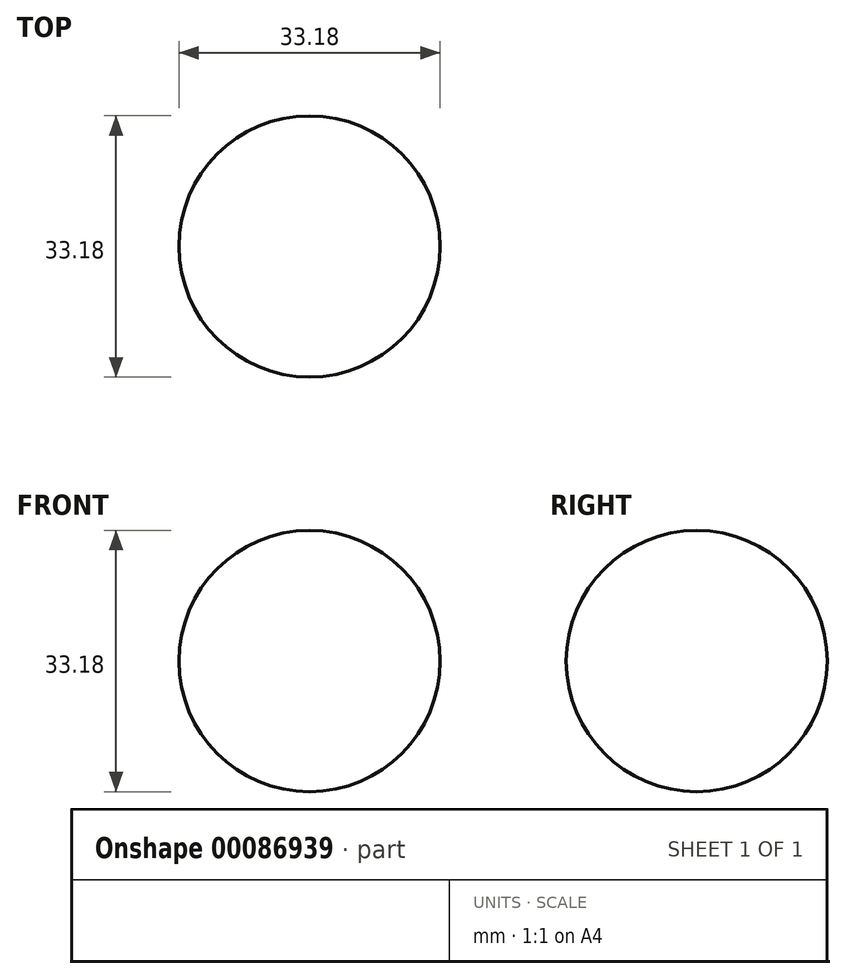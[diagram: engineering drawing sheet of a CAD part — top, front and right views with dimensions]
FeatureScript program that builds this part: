
annotation { "Feature Type Name" : "Feature", "Feature Type Description" : "" }
export const myFeature = defineFeature(function(context is Context, id is Id, definition is map)
    precondition{}
    {
        {
            var Q0;
            Q0=qCreatedBy(makeId("Front.planeOp"),FACE);
            var sketch = newSketch(context, id + "F0", { "sketchPlane" : qUnion([Q0])});
            skLineSegment(sketch, "E0", {"start": v(0, 0) * mm, "end": v(0, -229.17) * mm});
            skArc(sketch, "E1", {"start": v(0, -16.59) * mm, "mid": v(16.59, 0) * mm, "end": v(0, 16.59) * mm});
            skLineSegment(sketch, "E2", {"start": v(0, 0) * mm, "end": v(0, 16.59) * mm});
            skLineSegment(sketch, "E3", {"start": v(0, 0) * mm, "end": v(230.8, 0) * mm});
            skLineSegment(sketch, "E4.bottom", {"start": v(230.8, 13.81) * mm, "end": v(281.42, 13.81) * mm});
            skLineSegment(sketch, "E4.top", {"start": v(230.8, -19.65) * mm, "end": v(281.42, -19.65) * mm});
            skLineSegment(sketch, "E4.left", {"start": v(230.8, 13.81) * mm, "end": v(230.8, -19.65) * mm});
            skLineSegment(sketch, "E4.right", {"start": v(281.42, 13.81) * mm, "end": v(281.42, -19.65) * mm});
            skLineSegment(sketch, "E5.bottom", {"start": v(21.17, -229.17) * mm, "end": v(-17.32, -229.17) * mm});
            skLineSegment(sketch, "E5.top", {"start": v(21.17, -265.04) * mm, "end": v(-17.32, -265.04) * mm});
            skLineSegment(sketch, "E5.left", {"start": v(21.17, -229.17) * mm, "end": v(21.17, -265.04) * mm});
            skLineSegment(sketch, "E5.right", {"start": v(-17.32, -229.17) * mm, "end": v(-17.32, -265.04) * mm});
            skLineSegment(sketch, "E6.bottom", {"start": v(10.62, -238.4) * mm, "end": v(-8.54, -238.4) * mm});
            skLineSegment(sketch, "E6.top", {"start": v(10.62, -256.31) * mm, "end": v(-8.54, -256.31) * mm});
            skLineSegment(sketch, "E6.left", {"start": v(10.62, -238.4) * mm, "end": v(10.62, -256.31) * mm});
            skLineSegment(sketch, "E6.right", {"start": v(-8.54, -238.4) * mm, "end": v(-8.54, -256.31) * mm});
            skSolve(sketch);
        }
        {
            var Q0;
            Q0=qCreatedBy(makeId("Top.planeOp"),FACE);
            var Q1;
            Q1=sQuery(id+"F0.wireOp",VERTEX,"E0.end");
            cPlane(context, id + "F1", {"entities" : qUnion([Q0, Q1]), "cplaneType" : CPlaneType.PLANE_POINT, "offset" : 152.4 * mm, "width" : 152.4 * mm, "height" : 152.4 * mm});
        }
        {
            var Q0;
            {var subQ2=sQuery(id+"F0.wireOp",EDGE,"E1");Q0=makeQuery(id+"F0.imprint","IMPRINT",FACE,{"disambiguationData":[TD([[makeQuery(id+"F0.imprint","IMPRINT",EDGE,{"derivedFrom":subQ2}),1.0]])]});}
            var Q1;
            Q1=sQuery(id+"F0.wireOp",EDGE,"E0");
            revolve(context, id + "F2", {"entities" : qUnion([Q0]), "axis" : qUnion([Q1]), "revolveType" : RevolveType.FULL});
        }
    });
